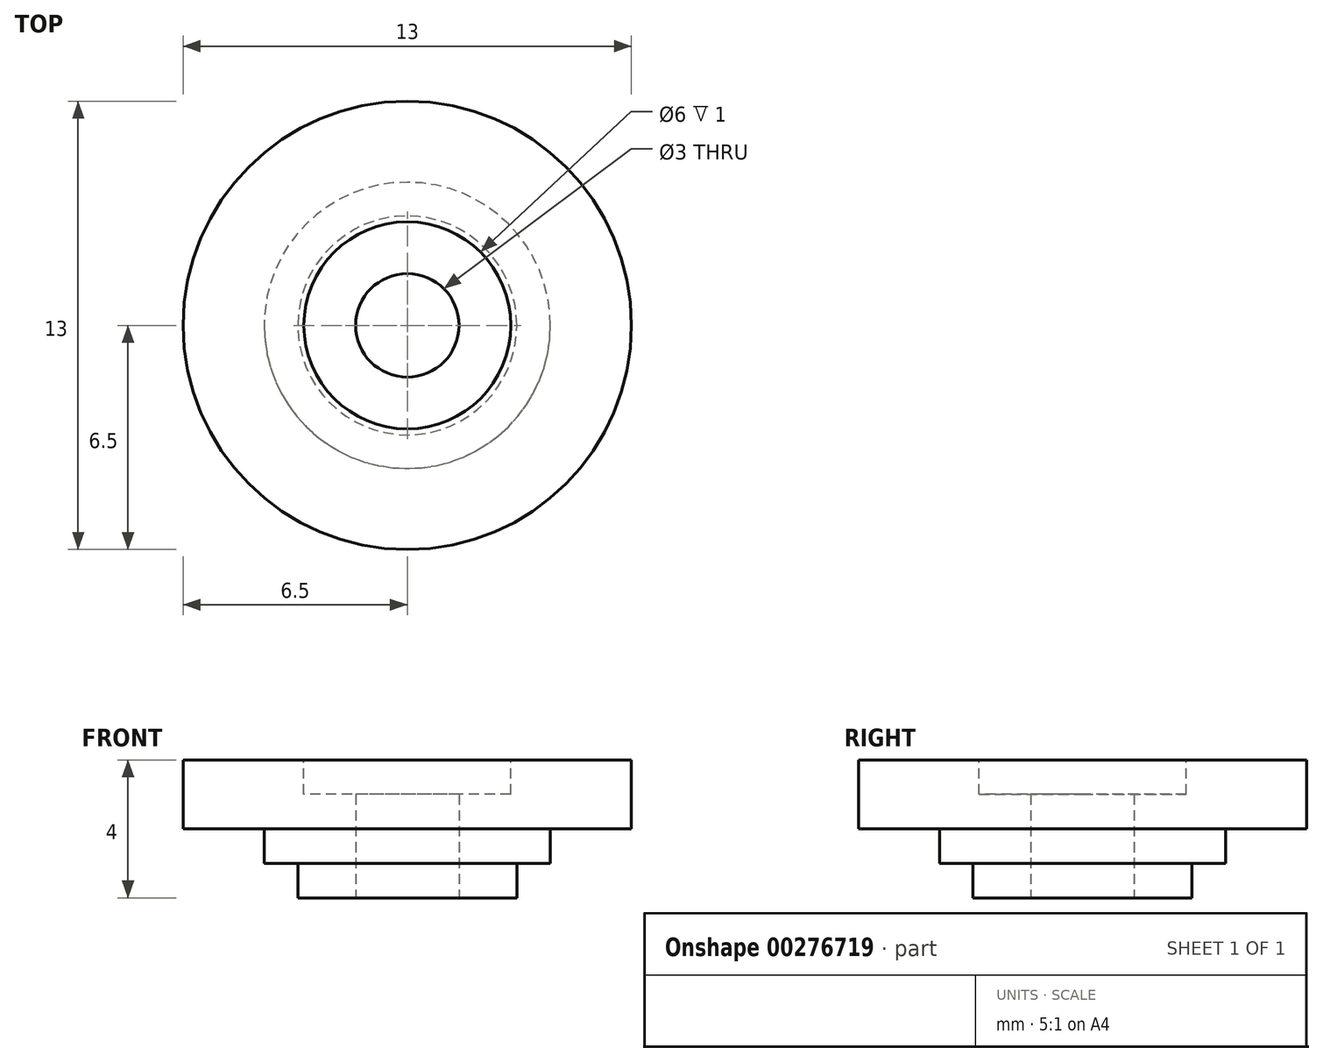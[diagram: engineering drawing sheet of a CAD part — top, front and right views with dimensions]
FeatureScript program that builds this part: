
annotation { "Feature Type Name" : "Feature", "Feature Type Description" : "" }
export const myFeature = defineFeature(function(context is Context, id is Id, definition is map)
    precondition{}
    {
        {
            var Q0;
            Q0=qCreatedBy(makeId("Top.planeOp"),FACE);
            var sketch = newSketch(context, id + "F0", { "sketchPlane" : qUnion([Q0])});
            skCircle(sketch, "E0", {"center": v(0, 0) * mm, "radius": 3.18 * mm});
            skSolve(sketch);
        }
        {
            var Q0;
            Q0 = qSketchRegion(id + "F0", true);
            extrude(context, id + "F1", {"entities" : qUnion([Q0]), "depth" : 2 * mm});
        }
        {
            var Q0;
            Q0=makeQuery(id+"F1.opExtrude","CAP_FACE",FACE,{"disambiguationData":[OSD([sQuery(id+"F0.wireOp",EDGE,"E0")])],"isStart":false});
            var sketch = newSketch(context, id + "F2", { "sketchPlane" : qUnion([Q0])});
            skCircle(sketch, "E1", {"center": v(0, 0) * mm, "radius": 6.5 * mm});
            skSolve(sketch);
        }
        {
            var Q0;
            Q0 = qSketchRegion(id + "F2", true);
            extrude(context, id + "F3", {"entities" : qUnion([Q0]), "operationType" : NewBodyOperationType.ADD, "depth" : 2 * mm});
        }
        {
            var Q0;
            Q0=makeQuery(id+"F3.opExtrude","CAP_FACE",FACE,{"disambiguationData":[OSD([sQuery(id+"F2.wireOp",EDGE,"E1")])],"isStart":false});
            var sketch = newSketch(context, id + "F4", { "sketchPlane" : qUnion([Q0])});
            skCircle(sketch, "E2", {"center": v(0, 0) * mm, "radius": 3 * mm});
            skSolve(sketch);
        }
        {
            var Q0;
            Q0=makeQuery(id+"F4.imprint","IMPRINT",FACE,{"disambiguationData":[TD([[makeQuery(id+"F4.imprint","IMPRINT",EDGE,{"derivedFrom":sQuery(id+"F4.wireOp",EDGE,"E2")}),1.0]])]});
            extrude(context, id + "F5", {"entities" : qUnion([Q0]), "operationType" : NewBodyOperationType.REMOVE, "oppositeDirection" : true, "depth" : 1 * mm});
        }
        {
            var Q0;
            Q0=makeQuery(id+"F1.opExtrude","CAP_FACE",FACE,{"disambiguationData":[OSD([sQuery(id+"F0.wireOp",EDGE,"E0")])],"isStart":true});
            var sketch = newSketch(context, id + "F6", { "sketchPlane" : qUnion([Q0])});
            skCircle(sketch, "E3", {"center": v(0, 0) * mm, "radius": 1.5 * mm});
            skSolve(sketch);
        }
        {
            var Q0;
            Q0 = qSketchRegion(id + "F6", true);
            extrude(context, id + "F7", {"entities" : qUnion([Q0]), "operationType" : NewBodyOperationType.REMOVE, "oppositeDirection" : true, "depth" : 25 * mm});
        }
        {
            var Q0;
            Q0=makeQuery(id+"F3.opExtrude","CAP_FACE",FACE,{"disambiguationData":[OSD([sQuery(id+"F2.wireOp",EDGE,"E1")])],"isStart":true});
            var sketch = newSketch(context, id + "F8", { "sketchPlane" : qUnion([Q0])});
            skCircle(sketch, "E4", {"center": v(0, 0) * mm, "radius": 4.15 * mm});
            skCircle(sketch, "E5.0", {"center": v(0, 0) * mm, "radius": 3.18 * mm});
            skSolve(sketch);
        }
        {
            var Q0;
            Q0 = qSketchRegion(id + "F8", true);
            extrude(context, id + "F9", {"entities" : qUnion([Q0]), "operationType" : NewBodyOperationType.ADD, "depth" : 1 * mm});
        }
    });
